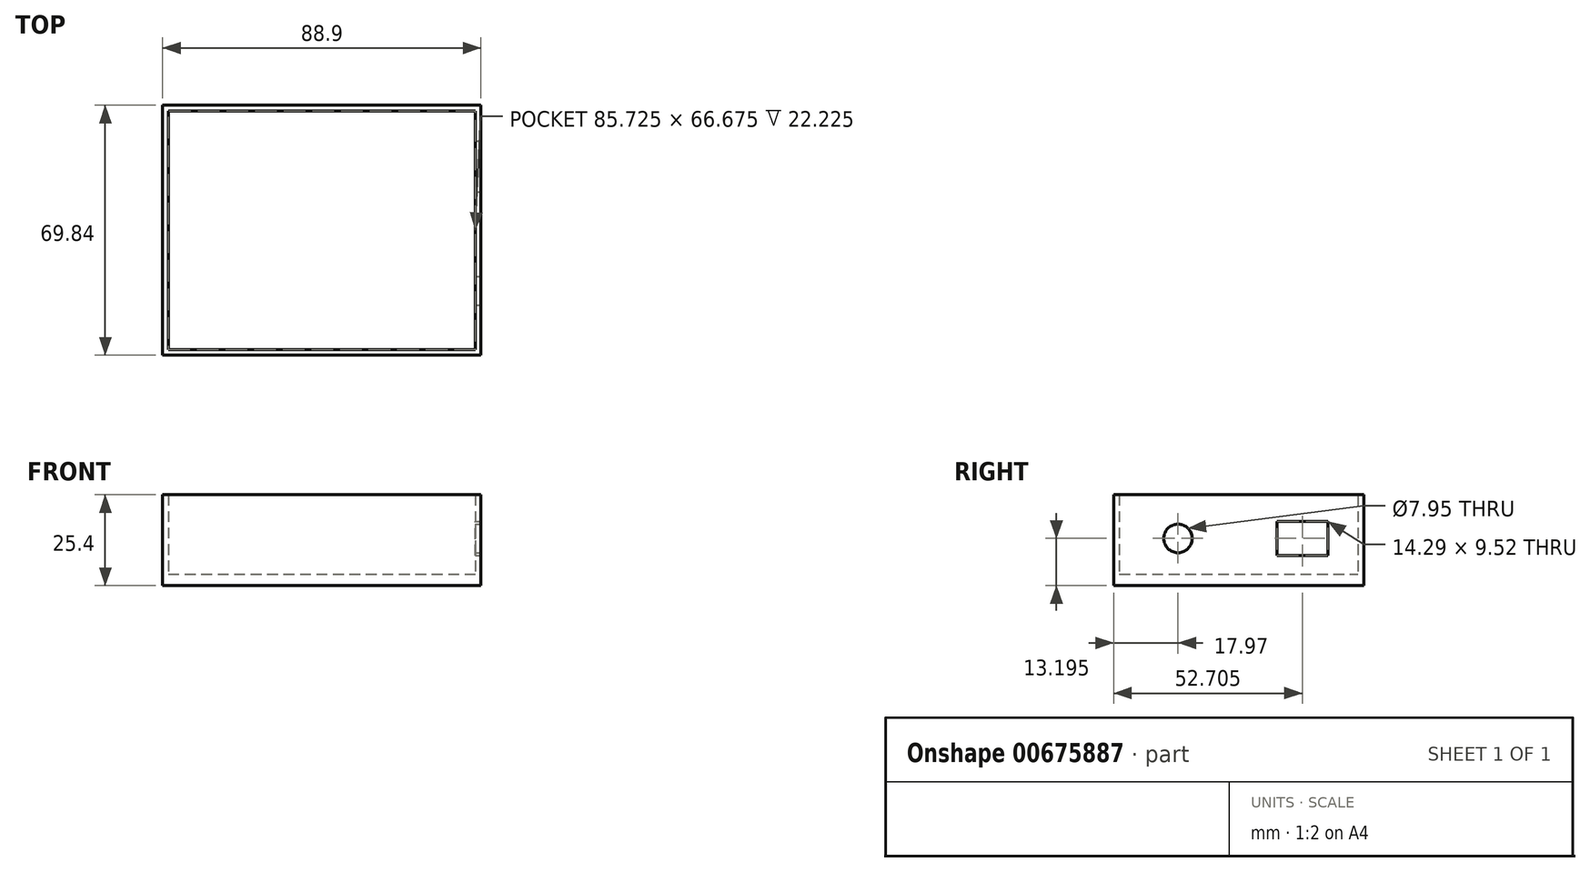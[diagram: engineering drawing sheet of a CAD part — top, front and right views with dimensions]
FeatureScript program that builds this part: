
annotation { "Feature Type Name" : "Feature", "Feature Type Description" : "" }
export const myFeature = defineFeature(function(context is Context, id is Id, definition is map)
    precondition{}
    {
        {
            var Q0;
            Q0=qCreatedBy(makeId("Top.planeOp"),FACE);
            var sketch = newSketch(context, id + "F0", { "sketchPlane" : qUnion([Q0])});
            skPoint(sketch, "E0.middle", {"position": v(0, 0) * mm});
            skLineSegment(sketch, "E1.bottom", {"start": v(44.45, 34.93) * mm, "end": v(-44.45, 34.92) * mm});
            skLineSegment(sketch, "E1.top", {"start": v(44.45, -34.92) * mm, "end": v(-44.45, -34.93) * mm});
            skLineSegment(sketch, "E1.left", {"start": v(44.45, 34.93) * mm, "end": v(44.45, -34.92) * mm});
            skLineSegment(sketch, "E1.right", {"start": v(-44.45, 34.92) * mm, "end": v(-44.45, -34.93) * mm});
            skLineSegment(sketch, "E2.bottom", {"start": v(-42.86, -33.34) * mm, "end": v(42.86, -33.34) * mm});
            skLineSegment(sketch, "E2.top", {"start": v(-42.86, 33.34) * mm, "end": v(42.86, 33.34) * mm});
            skLineSegment(sketch, "E2.left", {"start": v(-42.86, -33.34) * mm, "end": v(-42.86, 33.34) * mm});
            skLineSegment(sketch, "E2.right", {"start": v(42.86, -33.34) * mm, "end": v(42.86, 33.34) * mm});
            skSolve(sketch);
        }
        {
            var Q0;
            Q0 = qSketchRegion(id + "F0", true);
            extrude(context, id + "F1", {"entities" : qUnion([Q0]), "depth" : 25.4 * mm, "offsetDistance" : 25.4 * mm});
        }
        {
            var Q0;
            Q0=makeQuery(id+"F0.imprint","IMPRINT",FACE,{"disambiguationData":[TD([[makeQuery(id+"F0.imprint","IMPRINT",EDGE,{"derivedFrom":sQuery(id+"F0.wireOp",EDGE,"E2.bottom")}),1.0]])]});
            extrude(context, id + "F2", {"entities" : qUnion([Q0]), "operationType" : NewBodyOperationType.ADD, "depth" : 3.17 * mm, "offsetDistance" : 25.4 * mm});
        }
        {
            var Q0;
            Q0=makeQuery(id+"F1.opExtrude","SWEPT_FACE",FACE,{"disambiguationData":[OSD([sQuery(id+"F0.wireOp",EDGE,"E1.left")])]});
            var sketch = newSketch(context, id + "F3", { "sketchPlane" : qUnion([Q0])});
            skCircle(sketch, "E3", {"center": v(-16.95, 13.2) * mm, "radius": 3.97 * mm});
            skLineSegment(sketch, "E4.bottom", {"start": v(10.64, 8.43) * mm, "end": v(24.93, 8.43) * mm});
            skLineSegment(sketch, "E4.top", {"start": v(10.64, 17.96) * mm, "end": v(24.93, 17.96) * mm});
            skLineSegment(sketch, "E4.left", {"start": v(10.64, 8.43) * mm, "end": v(10.64, 17.96) * mm});
            skLineSegment(sketch, "E4.right", {"start": v(24.93, 8.43) * mm, "end": v(24.93, 17.96) * mm});
            skPoint(sketch, "E4.middle", {"position": v(17.78, 13.2) * mm});
            skSolve(sketch);
        }
        {
            var Q0;
            Q0=sQuery(id+"F3.wireOp",VERTEX,"E3.center");
            var Q1;
            Q1=makeQuery(id+"F1.opExtrude","SWEPT_BODY",BODY,{"disambiguationData":[OSD([sQuery(id+"F0.wireOp",EDGE,"E1.bottom"),sQuery(id+"F0.wireOp",EDGE,"E1.top"),sQuery(id+"F0.wireOp",EDGE,"E1.left"),sQuery(id+"F0.wireOp",EDGE,"E1.right"),sQuery(id+"F0.wireOp",EDGE,"E2.bottom"),sQuery(id+"F0.wireOp",EDGE,"E2.top"),sQuery(id+"F0.wireOp",EDGE,"E2.left"),sQuery(id+"F0.wireOp",EDGE,"E2.right")])]});
            hole(context, id + "F4", {"style" : HoleStyle.SIMPLE, "endStyle" : HoleEndStyle.BLIND, "holeDiameter" : 7.95 * mm, "majorDiameter" : 6.35 * mm, "holeDepth" : 12.7 * mm, "isTappedThrough" : true, "tappedDepth" : 12.7 * mm, "tapClearance" : 3, "locations" : qUnion([Q0]), "scope" : qUnion([Q1])});
        }
        {
            var Q0;
            Q0=makeQuery(id+"F3.imprint","IMPRINT",FACE,{"disambiguationData":[TD([[makeQuery(id+"F3.imprint","IMPRINT",EDGE,{"derivedFrom":sQuery(id+"F3.wireOp",EDGE,"E4.bottom")}),1.0]])]});
            extrude(context, id + "F5", {"entities" : qUnion([Q0]), "operationType" : NewBodyOperationType.REMOVE, "endBound" : BoundingType.UP_TO_NEXT, "oppositeDirection" : true, "depth" : 25.4 * mm, "offsetDistance" : 25.4 * mm});
        }
    });
